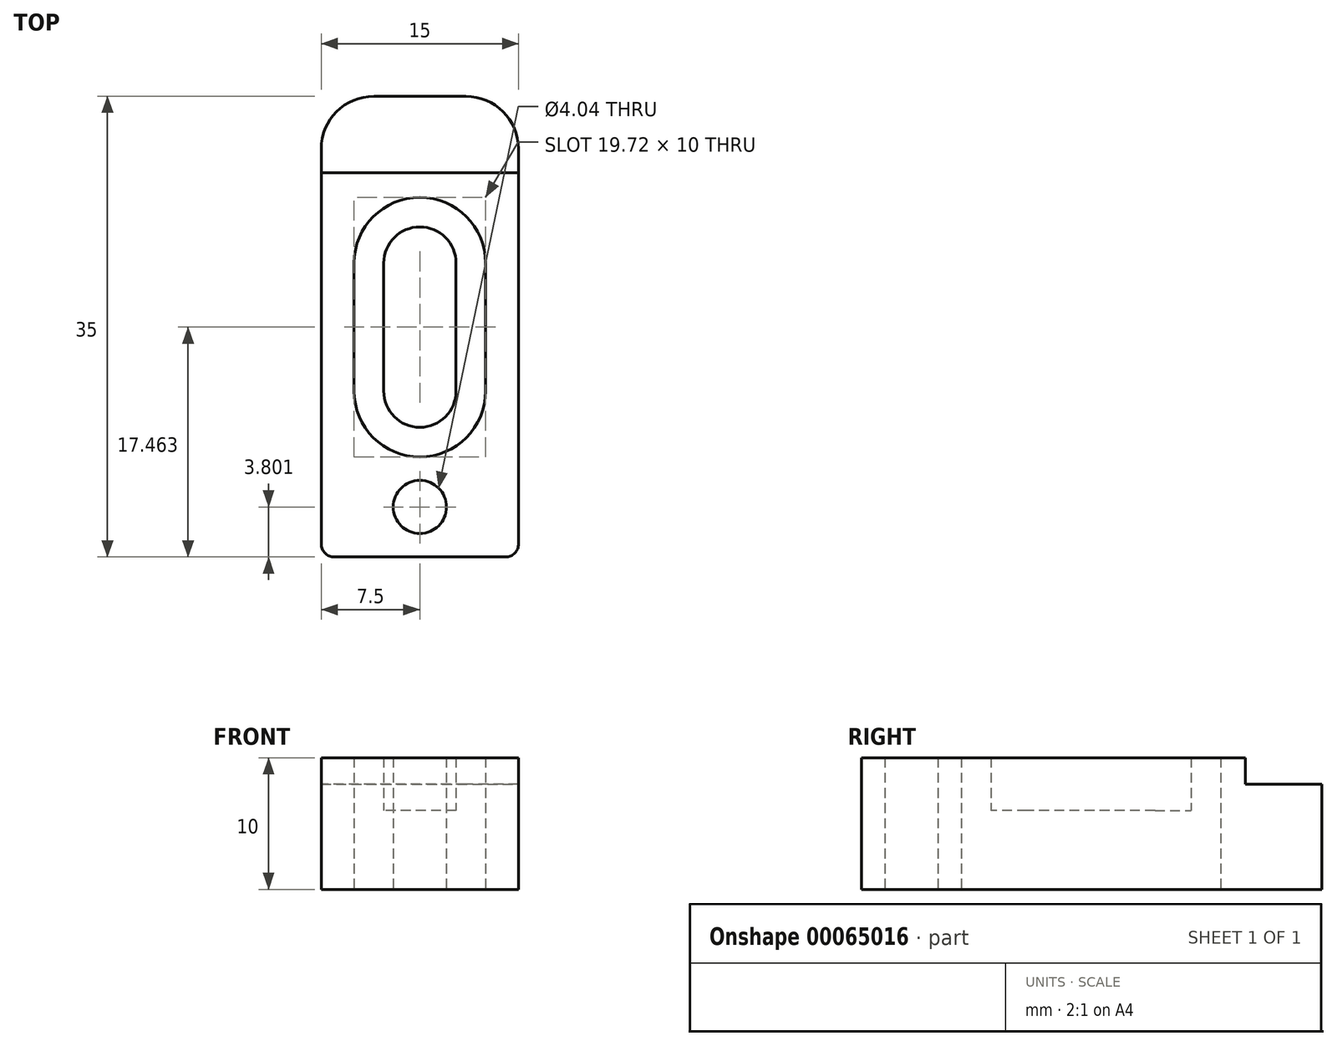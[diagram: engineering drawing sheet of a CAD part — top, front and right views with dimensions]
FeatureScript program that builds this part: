
annotation { "Feature Type Name" : "Feature", "Feature Type Description" : "" }
export const myFeature = defineFeature(function(context is Context, id is Id, definition is map)
    precondition{}
    {
        {
            var Q0;
            Q0=qCreatedBy(makeId("Top.planeOp"),FACE);
            var sketch = newSketch(context, id + "F0", { "sketchPlane" : qUnion([Q0])});
            skLineSegment(sketch, "E0.rect.bottom", {"start": v(6.5, -17.5) * mm, "end": v(-6.5, -17.5) * mm});
            skLineSegment(sketch, "E0.rect.top", {"start": v(3.5, 17.5) * mm, "end": v(-3.5, 17.5) * mm});
            skLineSegment(sketch, "E0.rect.left", {"start": v(7.5, -16.5) * mm, "end": v(7.5, 13.5) * mm});
            skLineSegment(sketch, "E0.rect.right", {"start": v(-7.5, -16.5) * mm, "end": v(-7.5, 13.5) * mm});
            skPoint(sketch, "E0.rect.middle", {"position": v(0, 0) * mm});
            skPoint(sketch, "E1.visualSharp", {"position": v(-7.5, 17.5) * mm});
            skArc(sketch, "E1.filletArc", {"start": v(-3.5, 17.5) * mm, "mid": v(-6.33, 16.33) * mm, "end": v(-7.5, 13.5) * mm});
            skPoint(sketch, "E2.visualSharp", {"position": v(7.5, 17.5) * mm});
            skArc(sketch, "E2.filletArc", {"start": v(7.5, 13.5) * mm, "mid": v(6.33, 16.33) * mm, "end": v(3.5, 17.5) * mm});
            skPoint(sketch, "E3.visualSharp", {"position": v(-7.5, -17.5) * mm});
            skArc(sketch, "E3.filletArc", {"start": v(-7.5, -16.5) * mm, "mid": v(-7.2, -17.2) * mm, "end": v(-6.5, -17.5) * mm});
            skPoint(sketch, "E4.visualSharp", {"position": v(7.5, -17.5) * mm});
            skArc(sketch, "E4.filletArc", {"start": v(6.5, -17.5) * mm, "mid": v(7.2, -17.2) * mm, "end": v(7.5, -16.5) * mm});
            skLineSegment(sketch, "E5", {"start": v(0, 4.82) * mm, "end": v(0, -4.9) * mm});
            skArc(sketch, "E6.0.startCap", {"start": v(-2.75, 4.82) * mm, "mid": v(0, 7.57) * mm, "end": v(2.75, 4.82) * mm});
            skArc(sketch, "E6.0.endCap", {"start": v(2.75, -4.9) * mm, "mid": v(0, -7.65) * mm, "end": v(-2.75, -4.9) * mm});
            skLineSegment(sketch, "E6.0.left", {"start": v(2.75, 4.82) * mm, "end": v(2.75, -4.9) * mm});
            skLineSegment(sketch, "E6.0.right", {"start": v(-2.75, 4.82) * mm, "end": v(-2.75, -4.9) * mm});
            skCircle(sketch, "E7", {"center": v(0, -13.7) * mm, "radius": 2.02 * mm});
            skArc(sketch, "E8.0.startCap", {"start": v(-5, 4.82) * mm, "mid": v(0, 9.82) * mm, "end": v(5, 4.82) * mm});
            skArc(sketch, "E8.0.endCap", {"start": v(5, -4.9) * mm, "mid": v(0, -9.9) * mm, "end": v(-5, -4.9) * mm});
            skLineSegment(sketch, "E8.0.left", {"start": v(5, 4.82) * mm, "end": v(5, -4.9) * mm});
            skLineSegment(sketch, "E8.0.right", {"start": v(-5, 4.82) * mm, "end": v(-5, -4.9) * mm});
            skLineSegment(sketch, "E9", {"start": v(0, -9.9) * mm, "end": v(0, -17.5) * mm, "construction": true});
            skSolve(sketch);
        }
        {
            var Q0;
            Q0=makeQuery(id+"F0.imprint","IMPRINT",FACE,{"disambiguationData":[TD([[makeQuery(id+"F0.imprint","IMPRINT",EDGE,{"derivedFrom":sQuery(id+"F0.wireOp",EDGE,"E0.rect.bottom")}),-1.0]])]});
            var Q1;
            Q1=makeQuery(id+"F0.imprint","IMPRINT",FACE,{"disambiguationData":[TD([[makeQuery(id+"F0.imprint","IMPRINT",EDGE,{"derivedFrom":sQuery(id+"F0.wireOp",EDGE,"E6.0.startCap")}),1.0]])]});
            extrude(context, id + "F1", {"entities" : qUnion([Q0, Q1]), "depth" : 10 * mm});
        }
        {
            var Q0;
            Q0=makeQuery(id+"F1.opExtrude","CAP_FACE",FACE,{"disambiguationData":[OSD([sQuery(id+"F0.wireOp",EDGE,"E0.rect.bottom"),sQuery(id+"F0.wireOp",EDGE,"E0.rect.top"),sQuery(id+"F0.wireOp",EDGE,"E0.rect.left"),sQuery(id+"F0.wireOp",EDGE,"E0.rect.right"),sQuery(id+"F0.wireOp",EDGE,"E1.filletArc"),sQuery(id+"F0.wireOp",EDGE,"E2.filletArc"),sQuery(id+"F0.wireOp",EDGE,"E3.filletArc"),sQuery(id+"F0.wireOp",EDGE,"E4.filletArc"),sQuery(id+"F0.wireOp",EDGE,"E6.0.startCap"),sQuery(id+"F0.wireOp",EDGE,"E6.0.endCap"),sQuery(id+"F0.wireOp",EDGE,"E6.0.left"),sQuery(id+"F0.wireOp",EDGE,"E6.0.right"),sQuery(id+"F0.wireOp",EDGE,"E7")])],"isStart":false});
            var sketch = newSketch(context, id + "F2", { "sketchPlane" : qUnion([Q0])});
            skLineSegment(sketch, "E10.bottom", {"start": v(-14.11, 11.7) * mm, "end": v(13.85, 11.7) * mm});
            skLineSegment(sketch, "E10.top", {"start": v(-14.11, 25.06) * mm, "end": v(13.85, 25.06) * mm});
            skLineSegment(sketch, "E10.left", {"start": v(-14.11, 11.7) * mm, "end": v(-14.11, 25.06) * mm});
            skLineSegment(sketch, "E10.right", {"start": v(13.85, 11.7) * mm, "end": v(13.85, 25.06) * mm});
            skSolve(sketch);
        }
        {
            var Q0;
            Q0 = qSketchRegion(id + "F2", true);
            extrude(context, id + "F3", {"entities" : qUnion([Q0]), "operationType" : NewBodyOperationType.REMOVE, "oppositeDirection" : true, "depth" : 2 * mm});
        }
        {
            var Q0;
            Q0=makeQuery(id+"F0.imprint","IMPRINT",FACE,{"disambiguationData":[TD([[makeQuery(id+"F0.imprint","IMPRINT",EDGE,{"derivedFrom":sQuery(id+"F0.wireOp",EDGE,"E6.0.startCap")}),1.0]])]});
            extrude(context, id + "F4", {"entities" : qUnion([Q0]), "operationType" : NewBodyOperationType.REMOVE, "depth" : 6 * mm});
        }
    });
